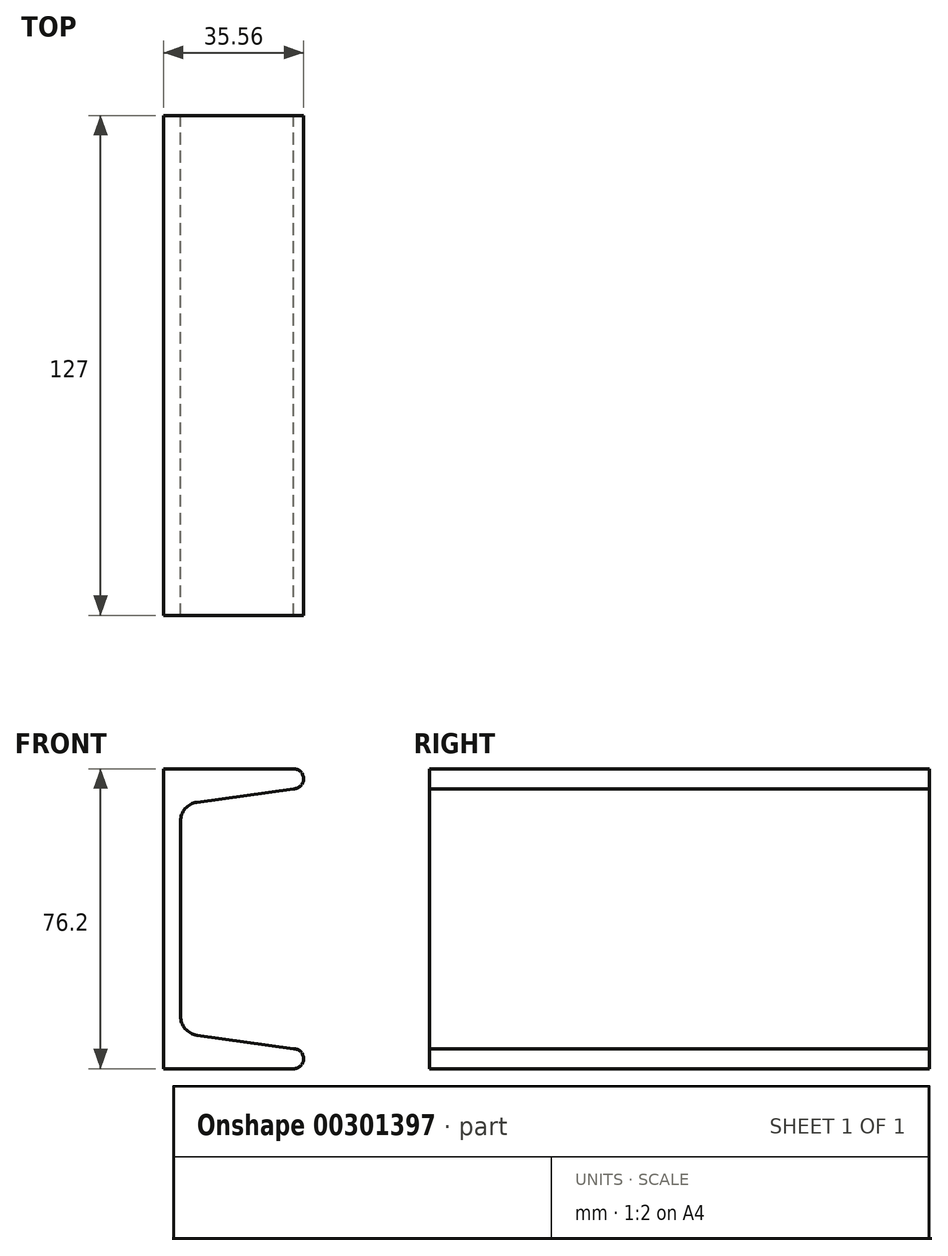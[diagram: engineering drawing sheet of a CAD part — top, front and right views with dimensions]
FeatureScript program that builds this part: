
annotation { "Feature Type Name" : "Feature", "Feature Type Description" : "" }
export const myFeature = defineFeature(function(context is Context, id is Id, definition is map)
    precondition{}
    {
        {
            var Q0;
            Q0=qCreatedBy(makeId("Front.planeOp"),FACE);
            var sketch = newSketch(context, id + "F0", { "sketchPlane" : qUnion([Q0])});
            skLineSegment(sketch, "E0", {"start": v(-24.06, 0) * mm, "end": v(-24.06, 38.1) * mm});
            skLineSegment(sketch, "E1", {"start": v(-24.06, 38.1) * mm, "end": v(8.96, 38.1) * mm});
            skArc(sketch, "E2", {"start": v(8.96, 38.1) * mm, "mid": v(11.5, 35.56) * mm, "end": v(8.96, 33.02) * mm});
            skLineSegment(sketch, "E3", {"start": v(8.96, 33.02) * mm, "end": v(-15.57, 29.6) * mm});
            skLineSegment(sketch, "E4", {"start": v(-19.75, 24.79) * mm, "end": v(-19.75, 0) * mm});
            skArc(sketch, "E5.MirrorCS", {"start": v(8.96, -38.1) * mm, "mid": v(11.5, -35.56) * mm, "end": v(8.96, -33.02) * mm});
            skLineSegment(sketch, "E6.MirrorCS", {"start": v(8.96, -33.02) * mm, "end": v(-15.57, -29.6) * mm});
            skLineSegment(sketch, "E7.MirrorCS", {"start": v(-19.75, -24.79) * mm, "end": v(-19.75, 0) * mm});
            skLineSegment(sketch, "E8.MirrorCS", {"start": v(-24.06, -38.1) * mm, "end": v(8.96, -38.1) * mm});
            skLineSegment(sketch, "E9.MirrorCS", {"start": v(-24.06, 0) * mm, "end": v(-24.06, -38.1) * mm});
            skPoint(sketch, "E10.visualSharp", {"position": v(-19.75, -29) * mm});
            skArc(sketch, "E10.filletArc", {"start": v(-19.75, -24.79) * mm, "mid": v(-18.55, -27.97) * mm, "end": v(-15.57, -29.6) * mm});
            skPoint(sketch, "E11.visualSharp", {"position": v(-19.75, 29) * mm});
            skArc(sketch, "E11.filletArc", {"start": v(-15.57, 29.6) * mm, "mid": v(-18.55, 27.97) * mm, "end": v(-19.75, 24.79) * mm});
            skSolve(sketch);
        }
        {
            var Q0;
            Q0 = qSketchRegion(id + "F0", true);
            extrude(context, id + "F1", {"entities" : qUnion([Q0]), "depth" : 127 * mm});
        }
    });
